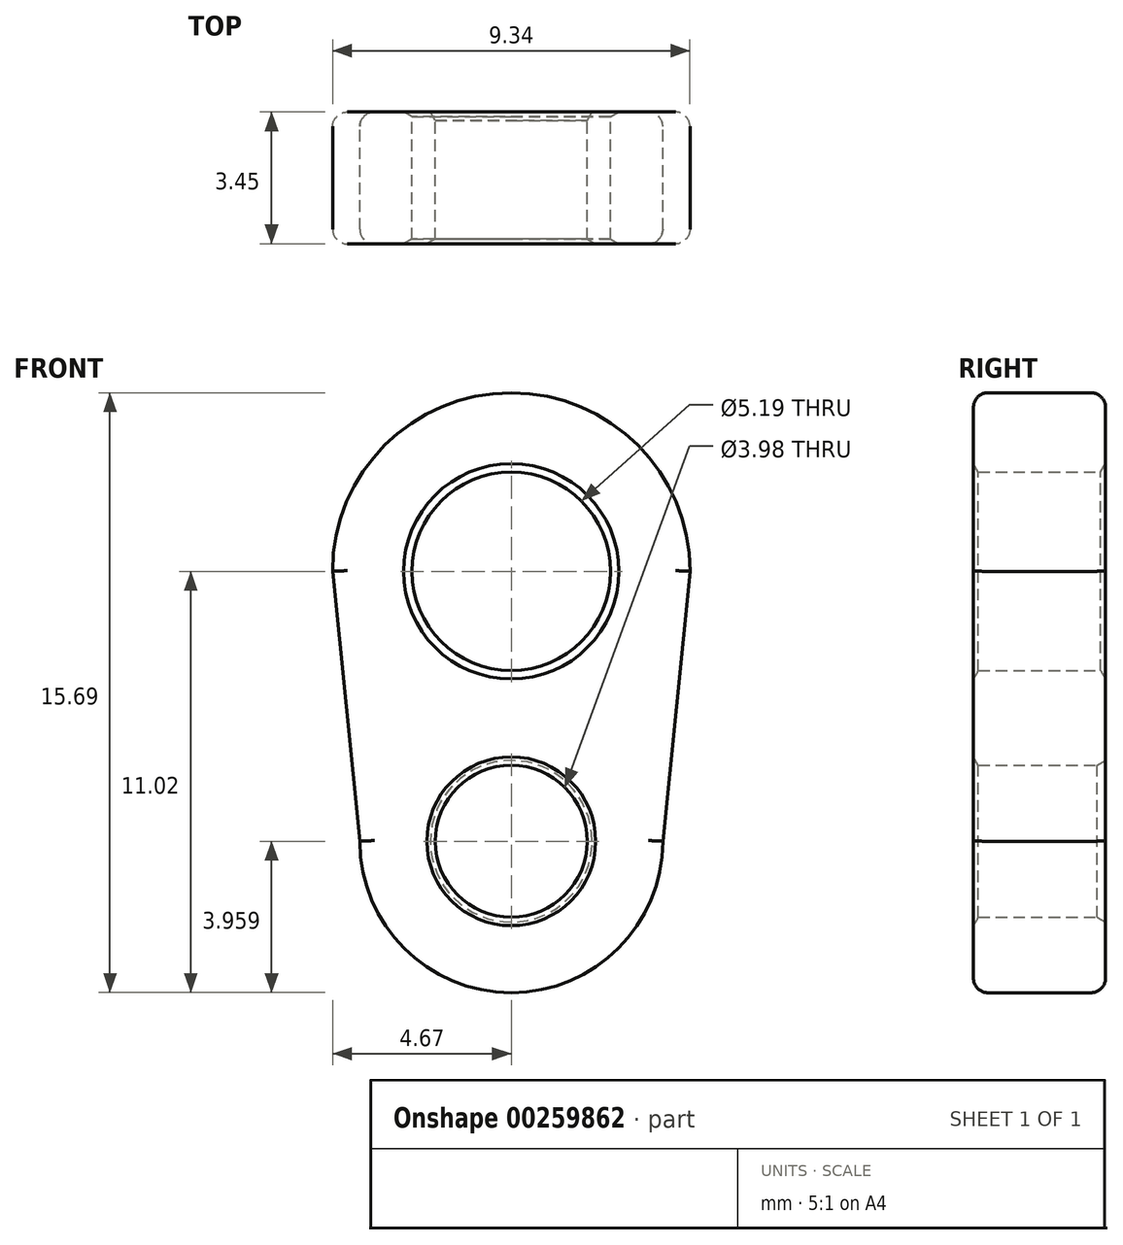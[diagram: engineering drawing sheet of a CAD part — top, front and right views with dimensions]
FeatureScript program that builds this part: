
annotation { "Feature Type Name" : "Feature", "Feature Type Description" : "" }
export const myFeature = defineFeature(function(context is Context, id is Id, definition is map)
    precondition{}
    {
        {
            var Q0;
            Q0=qCreatedBy(makeId("Front.planeOp"),FACE);
            var sketch = newSketch(context, id + "F0", { "sketchPlane" : qUnion([Q0])});
            skCircle(sketch, "E0", {"center": v(0, 0) * mm, "radius": 2.6 * mm});
            skCircle(sketch, "E1", {"center": v(0, -7.06) * mm, "radius": 1.99 * mm});
            skArc(sketch, "E2", {"start": v(-4.67, 0) * mm, "mid": v(0, 4.67) * mm, "end": v(4.67, 0) * mm});
            skArc(sketch, "E3", {"start": v(-3.96, -7.06) * mm, "mid": v(0, -11.02) * mm, "end": v(3.96, -7.06) * mm});
            skLineSegment(sketch, "E4", {"start": v(4.67, 0) * mm, "end": v(3.96, -7.06) * mm});
            skLineSegment(sketch, "E5", {"start": v(-3.96, -7.06) * mm, "end": v(-4.67, 0) * mm});
            skSolve(sketch);
        }
        {
            var Q0;
            Q0 = qSketchRegion(id + "F0", true);
            extrude(context, id + "F1", {"entities" : qUnion([Q0]), "depth" : 3.45 * mm});
        }
        {
            var Q0;
            Q0=makeQuery(id+"F1.opExtrude","CAP_EDGE",EDGE,{"disambiguationData":[OSD([sQuery(id+"F0.wireOp",EDGE,"E0")])],"isStart":false});
            var Q1;
            Q1=makeQuery(id+"F1.opExtrude","CAP_EDGE",EDGE,{"disambiguationData":[OSD([sQuery(id+"F0.wireOp",EDGE,"E1")])],"isStart":false});
            var Q2;
            Q2=makeQuery(id+"F1.opExtrude","CAP_EDGE",EDGE,{"disambiguationData":[OSD([sQuery(id+"F0.wireOp",EDGE,"E1")])],"isStart":true});
            var Q3;
            Q3=makeQuery(id+"F1.opExtrude","CAP_EDGE",EDGE,{"disambiguationData":[OSD([sQuery(id+"F0.wireOp",EDGE,"E0")])],"isStart":true});
            chamfer(context, id + "F2", {"entities" : qUnion([Q0, Q1, Q2, Q3]), "chamferType" : ChamferType.OFFSET_ANGLE, "width" : 0.13 * mm, "oppositeDirection" : false, "angle" : 60 * degree, "tangentPropagation" : true});
        }
        {
            var Q0;
            Q0=makeQuery(id+"F1.opExtrude","CAP_EDGE",EDGE,{"disambiguationData":[OSD([sQuery(id+"F0.wireOp",EDGE,"E2")])],"isStart":false});
            var Q1;
            Q1=makeQuery(id+"F1.opExtrude","CAP_EDGE",EDGE,{"disambiguationData":[OSD([sQuery(id+"F0.wireOp",EDGE,"E4")])],"isStart":false});
            var Q2;
            Q2=makeQuery(id+"F1.opExtrude","CAP_EDGE",EDGE,{"disambiguationData":[OSD([sQuery(id+"F0.wireOp",EDGE,"E3")])],"isStart":false});
            var Q3;
            Q3=makeQuery(id+"F1.opExtrude","CAP_EDGE",EDGE,{"disambiguationData":[OSD([sQuery(id+"F0.wireOp",EDGE,"E5")])],"isStart":false});
            var Q4;
            Q4=makeQuery(id+"F1.opExtrude","CAP_EDGE",EDGE,{"disambiguationData":[OSD([sQuery(id+"F0.wireOp",EDGE,"E4")])],"isStart":true});
            var Q5;
            Q5=makeQuery(id+"F1.opExtrude","CAP_EDGE",EDGE,{"disambiguationData":[OSD([sQuery(id+"F0.wireOp",EDGE,"E2")])],"isStart":true});
            var Q6;
            Q6=makeQuery(id+"F1.opExtrude","CAP_EDGE",EDGE,{"disambiguationData":[OSD([sQuery(id+"F0.wireOp",EDGE,"E3")])],"isStart":true});
            var Q7;
            Q7=makeQuery(id+"F1.opExtrude","CAP_EDGE",EDGE,{"disambiguationData":[OSD([sQuery(id+"F0.wireOp",EDGE,"E5")])],"isStart":true});
            fillet(context, id + "F3", {"entities" : qUnion([Q0, Q1, Q2, Q3, Q4, Q5, Q6, Q7]), "radius" : 0.38 * mm, "tangentPropagation" : true, "allowEdgeOverflow" : false});
        }
    });
